# Revit family: Soccer_Goals-Portable-Square-IPIbyBison
name_source: partatom
category: Specialty Equipment
units: mm (PartAtom-declared; Revit-internal decimal feet)

## family parameters
Always vertical = Yes
Classification Number = 23.40.50.34.14
Cut with Voids When Loaded = No
Enable Cutting in Views = No
Maintain Annotation Orientation = No
Part Type = Normal
Room Calculation Point = No
Round Connector Dimension = Use Diameter
Shared = No
Work Plane-Based = No

## types (6) — shared parameters
Ballasts = Ballasts - IPI by Bison - Sandbag
CAD Details = https://www.arcat.com
Default Elevation = 0' - 0"
Description = Square Soccer Goal Shootout Portable
Frame Material = Aluminum - IPI by Bison -
Keynote = 11 66 00
Manufacturer = IPI by Bison
Netting = Finish - IPI by Bison - White Netting
Product Page URL = https://www.arcat.com
Specification = https://www.arcat.com
Square Frame Color = Powder Coat - IPI by Bison - White
Top Depth = 4' - 0"
URL = https://ipibybison.com

## per-type parameters (varying)
| type | Ballasted | Base Depth | Goal Clearance | Height | Model |
| SC1865PA44E - Anchored | No | 6' - 6" | 18' - 6" | 6' - 6" | SC1865PA44E |
| SC2480PA44E - Anchored | No | 10' - 0" | 24' - 0" | 8' - 0" | SC2480PA44E |
| SC1865PA44NT - Ballasted | Yes | 6' - 6" | 18' - 6" | 6' - 6" | SC1865PA44NT |
| SC2170PA44NT - Ballasted | Yes | 7' - 0" | 21' - 0" | 7' - 0" | SC2170PA44NT |
| SC2170PA44E - Anchored | No | 7' - 0" | 21' - 0" | 7' - 0" | SC2170PA44E |
| SC2480PA44NT - Ballasted | Yes | 10' - 0" | 24' - 0" | 8' - 0" | SC2480PA44NT |

## geometry (parser evidence)
native form markers: Blend x2, Sweep x2
no freeform markers — native parametric forms only
